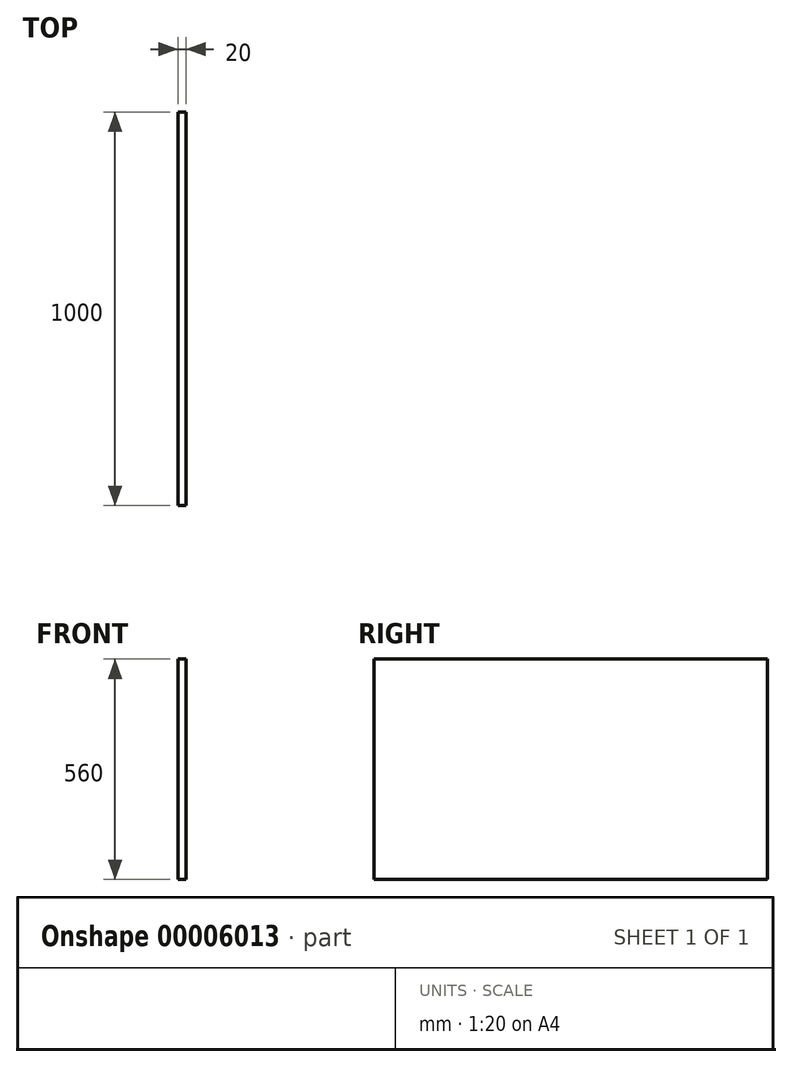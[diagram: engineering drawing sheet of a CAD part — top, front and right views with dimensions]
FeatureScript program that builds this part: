
annotation { "Feature Type Name" : "Feature", "Feature Type Description" : "" }
export const myFeature = defineFeature(function(context is Context, id is Id, definition is map)
    precondition{}
    {
        {
            var Q0;
            Q0=qCreatedBy(makeId("Right.planeOp"),FACE);
            var sketch = newSketch(context, id + "F0", { "sketchPlane" : qUnion([Q0])});
            skLineSegment(sketch, "E0.bottom", {"start": v(0, 0) * mm, "end": v(1000, 0) * mm});
            skLineSegment(sketch, "E0.top", {"start": v(0, 560) * mm, "end": v(1000, 560) * mm});
            skLineSegment(sketch, "E0.left", {"start": v(0, 0) * mm, "end": v(0, 560) * mm});
            skLineSegment(sketch, "E0.right", {"start": v(1000, 0) * mm, "end": v(1000, 560) * mm});
            skSolve(sketch);
        }
        {
            var Q0;
            Q0=makeQuery(id+"F0.imprint","IMPRINT",FACE,{"disambiguationData":[TD([[makeQuery(id+"F0.imprint","IMPRINT",EDGE,{"derivedFrom":sQuery(id+"F0.wireOp",EDGE,"E0.bottom")}),1.0]])]});
            extrude(context, id + "F1", {"entities" : qUnion([Q0]), "depth" : 20 * mm});
        }
    });
